# Revit family: Schnellkühler-Schockfroster Magnos Quereinschub - Eigen
name_source: partatom
category: Sonderausstattung
revit_build: Autodesk Revit 2015 (Build: 20140606_1530(x64)
units: mm (PartAtom-declared; Revit-internal decimal feet)

## types (4) — shared parameters
Anbau Hinten Tiefe = 38 mm  [stored 0.124672 ft]
Breite Unterbau = 217 mm  [stored 0.711942 ft]
DN Tauwasserabfluß = 20 mm  [stored 0.0656168 ft]
Deckplatte Stärke = 20 mm  [stored 0.0656168 ft]
Dichtung Stärke = 14 mm  [stored 0.0459318 ft]
Elektroanschluss Abstand Seite = 522 mm
Füße Abstand Hinten = 65 mm  [stored 0.213255 ft]
Füße Abstand Seiten = 65 mm  [stored 0.213255 ft]
Füße Abstand Vorne = 65 mm  [stored 0.213255 ft]
Hersteller = CoolCompact
Kältemittel = R404a
Material = Edelstahl AISI 304
Netzkabellänge = 2500 mm
Pole = 1
Scheinleistung = 0 VA
Tauwasserablauf Abstand von Vorne = 295 mm  [stored 0.967848 ft]
Tiefe Unterbau = 47 mm  [stored 0.154199 ft]
Türabstand Links = 5 mm  [stored 0.0164042 ft]
Türabstand Oben = 5 mm  [stored 0.0164042 ft]
Türabstand Rechts = 5 mm  [stored 0.0164042 ft]
Türabstand Unten = 5 mm  [stored 0.0164042 ft]
Türen Anzahl = 1
Türen Stärke = 64 mm  [stored 0.209974 ft]
Wandstärke Hinten = 60 mm  [stored 0.19685 ft]
Wandstärke Oben = 63 mm  [stored 0.206693 ft]
Wandstärke Seiten = 59 mm
Wandstärke Unten = 64 mm  [stored 0.209974 ft]

## per-type parameters (varying)
| type | Artikelnr. | Breite | Deckplatte Tiefe | Display Abstand Oben | Elektroanschluss Höhe | Kapazität | Korpus Höhe | Korpus Tiefe | Kälteleistung | Sockelhöhe | Spannung | Tauwasserabfluss Abstand Seite | Tauwasserabfluss Höhe | Türen Breite | Türen Höhe | Unterbau Höhe | Watt |
| 5x GN 1/1 EN6040 Quereinschub | SKFMEQ0511C-MS | 680 mm  [stored 2.23097 ft] | 652 mm  [stored 2.13911 ft] | 90 mm  [stored 0.295276 ft] | 230 mm  [stored 0.754593 ft] | 5 x GN1/1 oder 5 x EN6040 | 494 mm | 574 mm  [stored 1.8832 ft] | 1528 W -10°C VT / 599 W -30°C VT | 80 mm  [stored 0.262467 ft] | 230 V | 340 mm  [stored 1.11549 ft] | 80 mm  [stored 0.262467 ft] | 670 mm | 484 mm  [stored 1.58793 ft] | 256 mm  [stored 0.839895 ft] | 500 W |
| 8x GN 1/1 EN6040 Quereinschub | SKFMEQ0811C-MS | 790 mm  [stored 2.59186 ft] | 839 mm | 130 mm  [stored 0.426509 ft] | 430 mm | 8 x GN1/1 oder 8 x EN6040 | 799 mm  [stored 2.62139 ft] | 761 mm  [stored 2.49672 ft] | 1589 W -10°C VT / 620 W -30°C VT | 150 mm  [stored 0.492126 ft] | 230 V | 395 mm  [stored 1.29593 ft] | 150 mm  [stored 0.492126 ft] | 780 mm | 789 mm | 351 mm  [stored 1.15157 ft] | 600 W |
| 10x GN 1/1 EN6040 Quereinschub | SKFMEQ1011C-MS | 790 mm  [stored 2.59186 ft] | 761 mm  [stored 2.49672 ft] | 90 mm  [stored 0.295276 ft] | 630 mm  [stored 2.06693 ft] | 10 x GN1/1 oder 10 x EN6040 | 907 mm  [stored 2.97572 ft] | 761 mm  [stored 2.49672 ft] | 3219 W -10°C VT / 1160 W -30°C VT | 150 mm  [stored 0.492126 ft] | 230 V | 395 mm  [stored 1.29593 ft] | 150 mm  [stored 0.492126 ft] | 780 mm | 922 mm | 571 mm  [stored 1.87336 ft] | 900 W |
| 15x GN 1/1 EN6040 Quereinschub | SKFMEQ1511C-MS | 790 mm  [stored 2.59186 ft] | 761 mm  [stored 2.49672 ft] | 288 mm  [stored 0.944882 ft] | 630 mm  [stored 2.06693 ft] | 15 x GN1/1 oder 15 x EN6040 | 1228 mm | 761 mm  [stored 2.49672 ft] | 6844 W -10°C VT / 2218 W -30°C VT | 150 mm  [stored 0.492126 ft] | 400 V | 395 mm  [stored 1.29593 ft] | 150 mm  [stored 0.492126 ft] | 780 mm | 1243 mm | 590 mm  [stored 1.9357 ft] | 2300 W |

note: [stored X ft] marks values corroborated as IEEE doubles in the binary element streams (Revit-internal decimal feet)

## geometry (parser evidence)
native form markers: Blend x15, Sweep x3
no freeform markers — native parametric forms only
